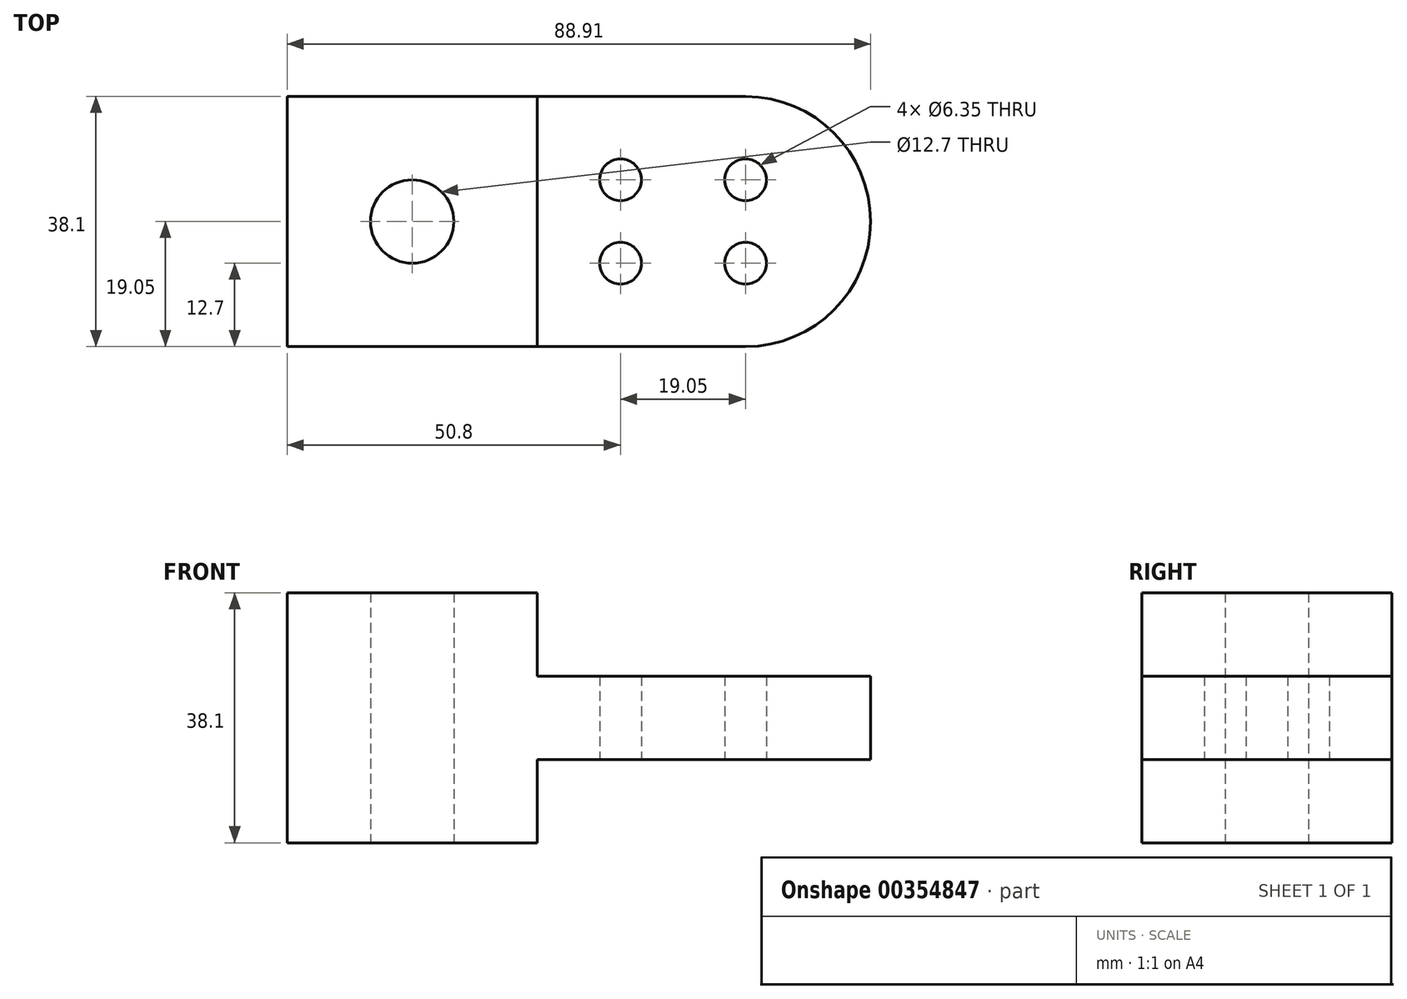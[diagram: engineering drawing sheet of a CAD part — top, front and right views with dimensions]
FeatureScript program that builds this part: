
annotation { "Feature Type Name" : "Feature", "Feature Type Description" : "" }
export const myFeature = defineFeature(function(context is Context, id is Id, definition is map)
    precondition{}
    {
        {
            var Q0;
            Q0=qCreatedBy(makeId("Top.planeOp"),FACE);
            var sketch = newSketch(context, id + "F0", { "sketchPlane" : qUnion([Q0])});
            skLineSegment(sketch, "E0.bottom", {"start": v(-19.05, 19.05) * mm, "end": v(19.05, 19.05) * mm});
            skLineSegment(sketch, "E0.top", {"start": v(-19.05, -19.05) * mm, "end": v(19.05, -19.05) * mm});
            skLineSegment(sketch, "E0.left", {"start": v(-19.05, 19.05) * mm, "end": v(-19.05, -19.05) * mm});
            skLineSegment(sketch, "E0.right", {"start": v(19.05, 19.05) * mm, "end": v(19.05, -19.05) * mm});
            skCircle(sketch, "E1", {"center": v(0, 0) * mm, "radius": 6.35 * mm});
            skSolve(sketch);
        }
        {
            var Q0;
            Q0 = qSketchRegion(id + "F0", true);
            extrude(context, id + "F1", {"entities" : qUnion([Q0]), "endBound" : BoundingType.SYMMETRIC, "depth" : 38.1 * mm});
        }
        {
            var Q0;
            Q0=qCreatedBy(makeId("Top.planeOp"),FACE);
            var sketch = newSketch(context, id + "F2", { "sketchPlane" : qUnion([Q0])});
            skLineSegment(sketch, "E2.0", {"start": v(19.05, 19.05) * mm, "end": v(19.05, -19.05) * mm});
            skLineSegment(sketch, "E3.bottom", {"start": v(19.05, 19.05) * mm, "end": v(50.81, 19.05) * mm});
            skLineSegment(sketch, "E3.top", {"start": v(19.05, -19.05) * mm, "end": v(50.81, -19.05) * mm});
            skArc(sketch, "E4", {"start": v(50.81, -19.05) * mm, "mid": v(69.86, 0) * mm, "end": v(50.81, 19.05) * mm});
            skCircle(sketch, "E5", {"center": v(31.75, 6.35) * mm, "radius": 3.18 * mm});
            skCircle(sketch, "E6.0.1.0", {"center": v(31.75, -6.35) * mm, "radius": 3.18 * mm});
            skCircle(sketch, "E6.1.0.0", {"center": v(50.8, 6.35) * mm, "radius": 3.18 * mm});
            skCircle(sketch, "E6.1.1.0", {"center": v(50.8, -6.35) * mm, "radius": 3.18 * mm});
            skLineSegment(sketch, "E6.direction1", {"start": v(31.75, 6.35) * mm, "end": v(50.8, 6.35) * mm, "construction": true});
            skLineSegment(sketch, "E6.direction2", {"start": v(31.75, 6.35) * mm, "end": v(31.75, -6.35) * mm, "construction": true});
            skSolve(sketch);
        }
        {
            var Q0;
            Q0 = qSketchRegion(id + "F2", true);
            extrude(context, id + "F3", {"entities" : qUnion([Q0]), "operationType" : NewBodyOperationType.ADD, "endBound" : BoundingType.SYMMETRIC, "depth" : 12.7 * mm});
        }
    });
